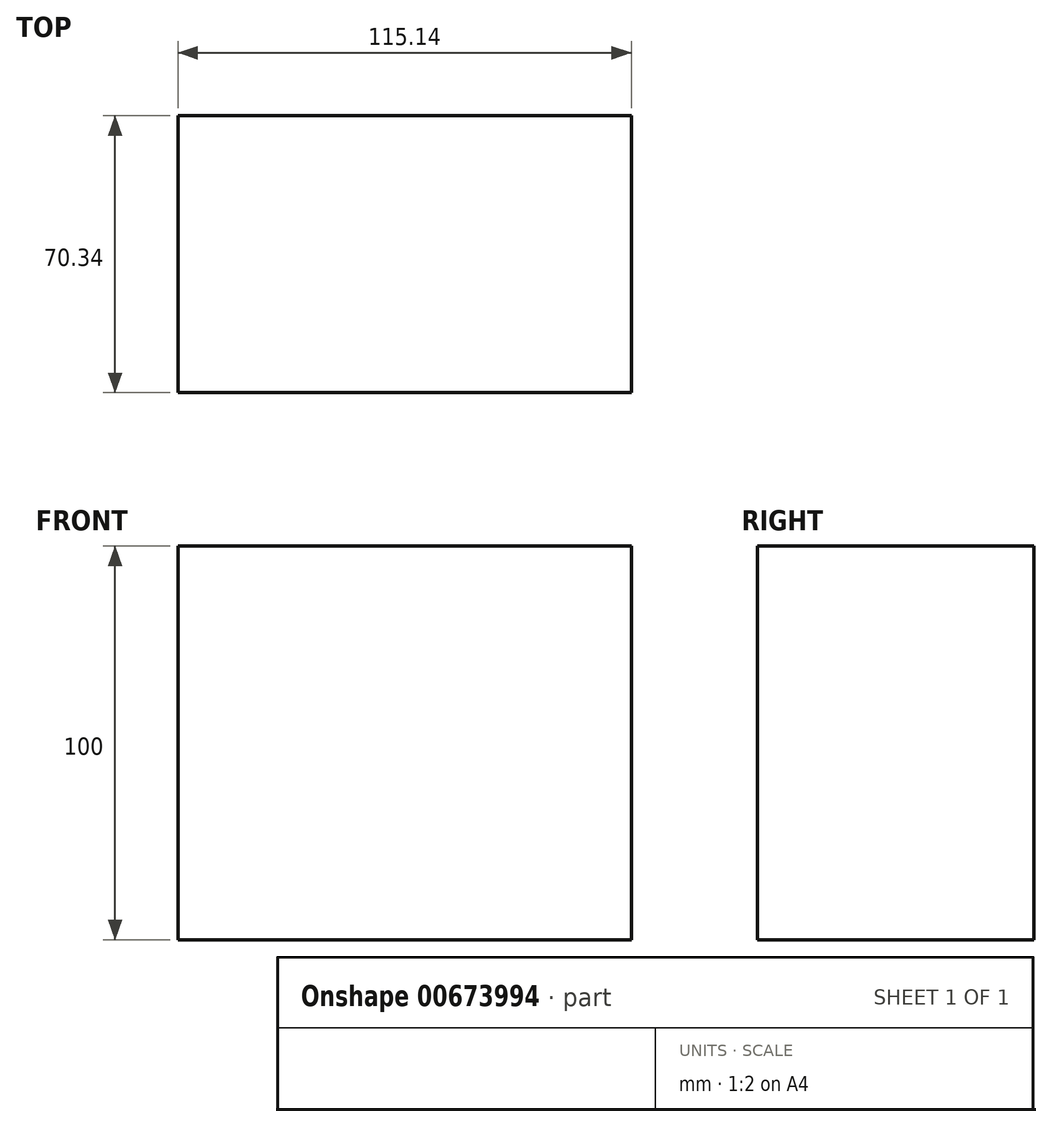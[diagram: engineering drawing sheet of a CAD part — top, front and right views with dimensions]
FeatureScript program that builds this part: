
annotation { "Feature Type Name" : "Feature", "Feature Type Description" : "" }
export const myFeature = defineFeature(function(context is Context, id is Id, definition is map)
    precondition{}
    {
        {
            var Q0;
            Q0=qCreatedBy(makeId("Top.planeOp"),FACE);
            var sketch = newSketch(context, id + "F0", { "sketchPlane" : qUnion([Q0])});
            skLineSegment(sketch, "E0.bottom", {"start": v(-37.87, 23.5) * mm, "end": v(77.27, 23.5) * mm});
            skLineSegment(sketch, "E0.top", {"start": v(-37.87, -46.84) * mm, "end": v(77.27, -46.84) * mm});
            skLineSegment(sketch, "E0.left", {"start": v(-37.87, 23.5) * mm, "end": v(-37.87, -46.84) * mm});
            skLineSegment(sketch, "E0.right", {"start": v(77.27, 23.5) * mm, "end": v(77.27, -46.84) * mm});
            skSolve(sketch);
        }
        {
            var Q0;
            Q0=makeQuery(id+"F0.imprint","IMPRINT",FACE,{"disambiguationData":[TD([[makeQuery(id+"F0.imprint","IMPRINT",EDGE,{"derivedFrom":sQuery(id+"F0.wireOp",EDGE,"E0.bottom")}),-1.0]])]});
            extrude(context, id + "F1", {"entities" : qUnion([Q0]), "depth" : 100 * mm, "offsetDistance" : 25.4 * mm});
        }
    });
